# Revit family: Hekatron_Feststellanlagen_ORS 142 Ex_DE_22.01
name_source: partatom
category: Brandmelder
revit_build: Autodesk Revit 2018 (Build: 20190510_1515(x64)
units: mm (PartAtom-declared; Revit-internal decimal feet)

## family parameters
Basisbauteil = Fläche
Beim Laden mit Abzugskörper schneiden = Nein
Bemaßung runder Anschluss = Durchmesser verwenden
Beschriftungsausrichtung beibehalten = Ja
Gemeinsam genutzt = Nein
OmniClass-Nummer = 23.85.30.21
OmniClass-Titel = Environmental Detection/Registration
Raumberechnungspunkt = Nein
Teiletyp = Normal

## types (1)
- ORS 142 Ex
    Bauartgenehmigungen = Z-6.500-2405, Z-6.500-2401, Z-6.500-2300, Z-6.500-2311, Z-6.500-2388, Z-6.500-2340, Z-6.500-2359, Z-6.500-2393, Z-6.500-2394, Z-6.500-2415, Z-6.500-2381, Z-6.500-2386, Z-6.500-2407, Z-6.500-2365, Z-6.500-2403, Z-6.500-2419, Z-6.500-2441, Z-6.500-2442, Z-6.500-2400, Z-6.500-2436, Z-6.500-2451, Z-6.500-2452, Z-6.500-2499, Z-6.500-2515
    Beschreibung = Optischer Rauchschalter zum Einsatz in Feststellanlagen oder anderen Anwendungen in explosionsgefährdeten Bereichen der Zonen 1, 2 und 22 gemäß ATEX.
    Betriebsspannung = 20 bis 28 V DC
    Durchmesser (mm) = 80.0
    Ex-Zonen = 1, 2, 22
    Farbe = Melder weiß, ähnlich RAL 9010
Anschlussbox schwarz
    Funktionsprinzip = optisch
    Hersteller = Hekatron
    Höhe (mm) = 66.0
    Kabeleinführung = Seite
    Link zu Ausschreibungstext = https://www.meinhplus.de
    Link zu Produktinformation = https://www.hekatron-planungstools.de
    Link zu ausschreiben.de = http://www.ausschreiben.de
    Link zum Datenblatt = https://www.hekatron-planungstools.de
    Material = PC
    Modell = ORS 142 Ex
    Montageart = Aufputz
    Nettogewicht (g) = 1052.0
    Schutzart = IP 54
    Stromaufnahme = max. 12mA
    Tiefe (mm) = 123.0
    Typenkommentare = Optischer Rauchschalter, Ex-Ausführung
    UB A&S Artikel Nummer = 5000590-0201
    URL = https://www.hekatron-brandschutz.de
    Version des BIM Objektes = 22.01
    Vorgabe-Ansicht = 1200 mm
    Zulässige Umgebungstemperatur = -20 °C bis +70 °C

## geometry (parser evidence)
native form markers: Extrusion x1, Sweep x2
no freeform markers — native parametric forms only
